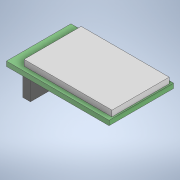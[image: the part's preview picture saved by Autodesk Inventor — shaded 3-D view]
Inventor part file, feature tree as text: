
AUTODESK INVENTOR PART (.ipt)
format: ipt  version: 2022 (Build 260153000, 153)  size: 129,536 bytes
history: native  units: mm
features: extrude x3, sketch x3, other x1
ambient origin geometry x8: Origin, YZ Plane, XZ Plane, XY Plane, X Axis, Y Axis, Z Axis, Center Point
bodies: Body1 (feature_tree)
feature tree (7):
  other  "ソリッド1"
  extrude  "押し出し1"  Depth=35.0mm
  extrude  "押し出し2"  Depth=22.0mm
  extrude  "押し出し3"  Depth=1.6mm TaperAngle=0.0deg
  sketch  "スケッチ1"
  sketch  "スケッチ2"
  sketch  "スケッチ3"
